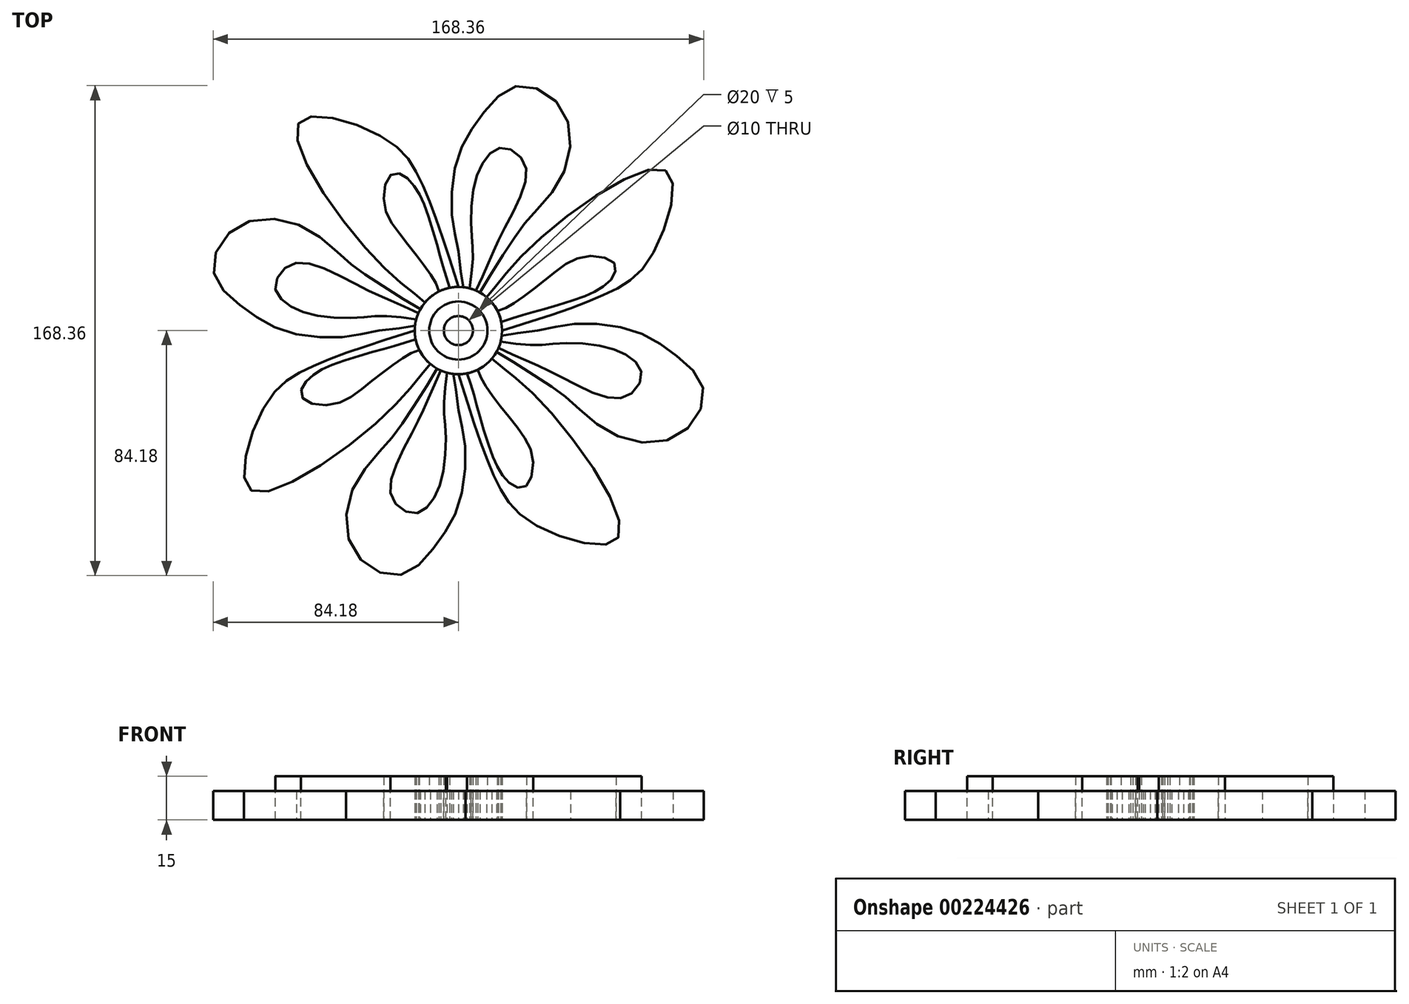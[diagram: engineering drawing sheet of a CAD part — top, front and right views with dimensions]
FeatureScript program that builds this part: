
annotation { "Feature Type Name" : "Feature", "Feature Type Description" : "" }
export const myFeature = defineFeature(function(context is Context, id is Id, definition is map)
    precondition{}
    {
        {
            var Q0;
            Q0=qCreatedBy(makeId("Top.planeOp"),FACE);
            var sketch = newSketch(context, id + "F0", { "sketchPlane" : qUnion([Q0])});
            skCircle(sketch, "E0", {"center": v(0, 0) * mm, "radius": 15 * mm});
            skFitSpline(sketch, "E1", {"points": [v(-15, 0) * mm, v(-34.32, -6.21) * mm, v(-53.36, -13.89) * mm, v(-66.7, -26.32) * mm, v(-71.4, -54.77) * mm, v(-26.4, -30.16) * mm, v(-9.67, -11.46) * mm], "startDerivative": vector(-62.7, -20.91) * mm, "endDerivative": vector(65.85, 73.3) * mm});
            skCircle(sketch, "E2", {"center": v(0, 0) * mm, "radius": 10 * mm});
            skCircle(sketch, "E3", {"center": v(0, 0) * mm, "radius": 5 * mm});
            skFitSpline(sketch, "E4", {"points": [v(-7.37, -13.06) * mm, v(-17.25, -28.89) * mm, v(-24.4, -38.71) * mm, v(-35.96, -53.83) * mm, v(-35.96, -75.61) * mm, v(-20.4, -84.06) * mm, v(-8.13, -74.16) * mm, v(0, -60.17) * mm, v(2.28, -40.04) * mm, v(0, -27.2) * mm, v(-1.72, -14.9) * mm], "startDerivative": vector(-50.93, -98.92) * mm, "endDerivative": vector(-27, 84.6) * mm});
            skFitSpline(sketch, "E5", {"points": [v(-14.7, -2.98) * mm, v(-22.31, -5.37) * mm, v(-30.14, -7.54) * mm, v(-42.46, -11.46) * mm, v(-48.86, -14.59) * mm, v(-53.36, -18.92) * mm, v(-53.36, -23.39) * mm, v(-43.5, -25.48) * mm, v(-34.32, -20.99) * mm, v(-25.3, -13.89) * mm, v(-18.05, -8.8) * mm, v(-13.43, -6.68) * mm], "startDerivative": vector(-85.61, -26.94) * mm, "endDerivative": vector(67.68, 16) * mm});
            skFitSpline(sketch, "E6", {"points": [v(-6.02, -13.74) * mm, v(-11.23, -25.4) * mm, v(-15.04, -33.55) * mm, v(-22.31, -48.7) * mm, v(-22.31, -58.4) * mm, v(-15.04, -62.9) * mm, v(-9.18, -58.87) * mm, v(-5.21, -48.7) * mm, v(-4.43, -33.94) * mm, v(-5.02, -26.56) * mm, v(-3.85, -14.5) * mm], "startDerivative": vector(-51.58, -111.99) * mm, "endDerivative": vector(16.35, 118.82) * mm});
            skSolve(sketch);
        }
        {
            var Q0;
            {var subQ0=sQuery(id+"F0.wireOp",EDGE,"E1");Q0=makeQuery(id+"F0.imprint","IMPRINT",FACE,{"disambiguationData":[TD([[makeQuery(id+"F0.imprint","IMPRINT",EDGE,{"derivedFrom":subQ0}),1.0]])]});}
            extrude(context, id + "F1", {"entities" : qUnion([Q0]), "depth" : 10 * mm});
        }
        {
            var Q0;
            {var subQ0=sQuery(id+"F0.wireOp",EDGE,"E1");var subQ1=sQuery(id+"F0.wireOp",EDGE,"E0");var subQ2=makeQuery(id+"F0.imprint","INTERSECT",VERTEX,{"disambiguationData":[OD(0.0)],"derivedFrom":[subQ1,subQ0]});Q0=makeQuery(id+"F0.imprint","IMPRINT",FACE,{"disambiguationData":[TD([[makeQuery(id+"F0.imprint","IMPRINT",EDGE,{"disambiguationData":[TD([[subQ2,-1.0]])],"derivedFrom":subQ1}),1.0]])]});}
            extrude(context, id + "F2", {"entities" : qUnion([Q0]), "depth" : 15 * mm});
        }
        {
            var Q0;
            Q0=makeQuery(id+"F1.opExtrude","SWEPT_BODY",BODY,{"disambiguationData":[OSD([sQuery(id+"F0.wireOp",EDGE,"E0"),sQuery(id+"F0.wireOp",EDGE,"E1"),sQuery(id+"F0.wireOp",EDGE,"E5")])]});
            var Q1;
            Q1=makeQuery(id+"F2.opExtrude","CAP_EDGE",EDGE,{"disambiguationData":[OSD([sQuery(id+"F0.wireOp",EDGE,"E0")])],"isStart":false});
            circularPattern(context, id + "F3", {"entities" : qUnion([Q0]), "axis" : qUnion([Q1]), "angle" : 360 * degree, "instanceCount" : 4, "equalSpace" : true});
        }
        {
            var Q0;
            {var subQ0=sQuery(id+"F0.wireOp",EDGE,"E4");Q0=makeQuery(id+"F0.imprint","IMPRINT",FACE,{"disambiguationData":[TD([[makeQuery(id+"F0.imprint","IMPRINT",EDGE,{"derivedFrom":subQ0}),1.0]])]});}
            extrude(context, id + "F4", {"entities" : qUnion([Q0]), "depth" : 10 * mm});
        }
        {
            var Q0;
            Q0=makeQuery(id+"F4.opExtrude","SWEPT_BODY",BODY,{"disambiguationData":[OSD([sQuery(id+"F0.wireOp",EDGE,"E0"),sQuery(id+"F0.wireOp",EDGE,"E4")])]});
            var Q1;
            Q1=sQuery(id+"F0.wireOp",EDGE,"E0");
            circularPattern(context, id + "F5", {"entities" : qUnion([Q0]), "axis" : qUnion([Q1]), "angle" : 360 * degree, "instanceCount" : 4, "oppositeDirection" : true, "equalSpace" : true});
        }
        {
            var Q0;
            Q0=makeQuery(id+"F0.imprint","IMPRINT",FACE,{"disambiguationData":[TD([[makeQuery(id+"F0.imprint","IMPRINT",EDGE,{"derivedFrom":sQuery(id+"F0.wireOp",EDGE,"E2")}),1.0]])]});
            extrude(context, id + "F6", {"entities" : qUnion([Q0]), "operationType" : NewBodyOperationType.ADD, "depth" : 10 * mm});
        }
        {
            var Q0;
            {var subQ0=sQuery(id+"F0.wireOp",EDGE,"E5");Q0=makeQuery(id+"F0.imprint","IMPRINT",FACE,{"disambiguationData":[TD([[makeQuery(id+"F0.imprint","IMPRINT",EDGE,{"derivedFrom":subQ0}),1.0]])]});}
            extrude(context, id + "F7", {"entities" : qUnion([Q0]), "depth" : 15 * mm});
        }
        {
            var Q0;
            Q0=makeQuery(id+"F7.opExtrude","SWEPT_BODY",BODY,{"disambiguationData":[OSD([sQuery(id+"F0.wireOp",EDGE,"E0"),sQuery(id+"F0.wireOp",EDGE,"E5")])]});
            var Q1;
            Q1=sQuery(id+"F0.wireOp",EDGE,"E2");
            circularPattern(context, id + "F8", {"entities" : qUnion([Q0]), "axis" : qUnion([Q1]), "angle" : 360 * degree, "instanceCount" : 4, "equalSpace" : true});
        }
        {
            var Q0;
            {var subQ0=sQuery(id+"F0.wireOp",EDGE,"E6");Q0=makeQuery(id+"F0.imprint","IMPRINT",FACE,{"disambiguationData":[TD([[makeQuery(id+"F0.imprint","IMPRINT",EDGE,{"derivedFrom":subQ0}),1.0]])]});}
            extrude(context, id + "F9", {"entities" : qUnion([Q0]), "depth" : 15 * mm});
        }
        {
            var Q0;
            Q0=makeQuery(id+"F9.opExtrude","SWEPT_BODY",BODY,{"disambiguationData":[OSD([sQuery(id+"F0.wireOp",EDGE,"E0"),sQuery(id+"F0.wireOp",EDGE,"E6")])]});
            var Q1;
            Q1=sQuery(id+"F0.wireOp",EDGE,"E0");
            circularPattern(context, id + "F10", {"entities" : qUnion([Q0]), "axis" : qUnion([Q1]), "angle" : 360 * degree, "instanceCount" : 4, "equalSpace" : true});
        }
    });
